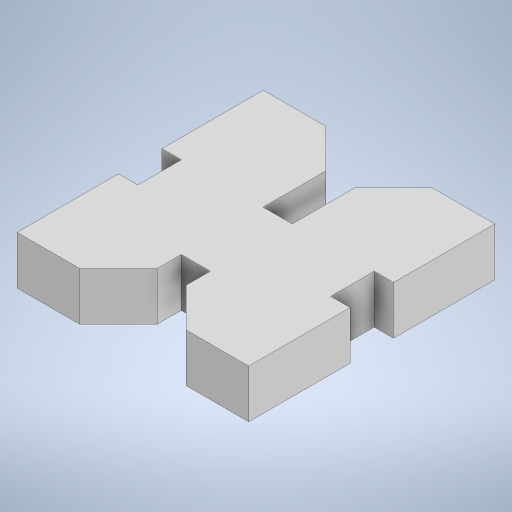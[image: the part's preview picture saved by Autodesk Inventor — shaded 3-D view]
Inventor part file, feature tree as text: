
AUTODESK INVENTOR PART (.ipt)
format: ipt  version: 2024 (Build 280153000, 153)  size: 240,128 bytes
history: native  units: mm
features: extrude x1, sketch x1
ambient origin geometry x8: Origin, YZ Plane, XZ Plane, XY Plane, X Axis, Y Axis, Z Axis, Center Point
bodies: Volumenkörper1 (feature_tree)
feature tree (2):
  extrude  "Extrusion1"  Depth=9.0mm
  sketch  "Skizze1"  dims[d0=21.0mm d1=9.0mm d2=21.0mm d3=21.0mm d4=21.0mm d5=4.0mm d6=4.0mm d7=13.0mm d8=22.0mm d9=13.0mm d10=21.0mm d11=135.0deg d12=135.0deg d13=45.0deg d14=45.0deg d15=10.0mm d16=0.0mm]
